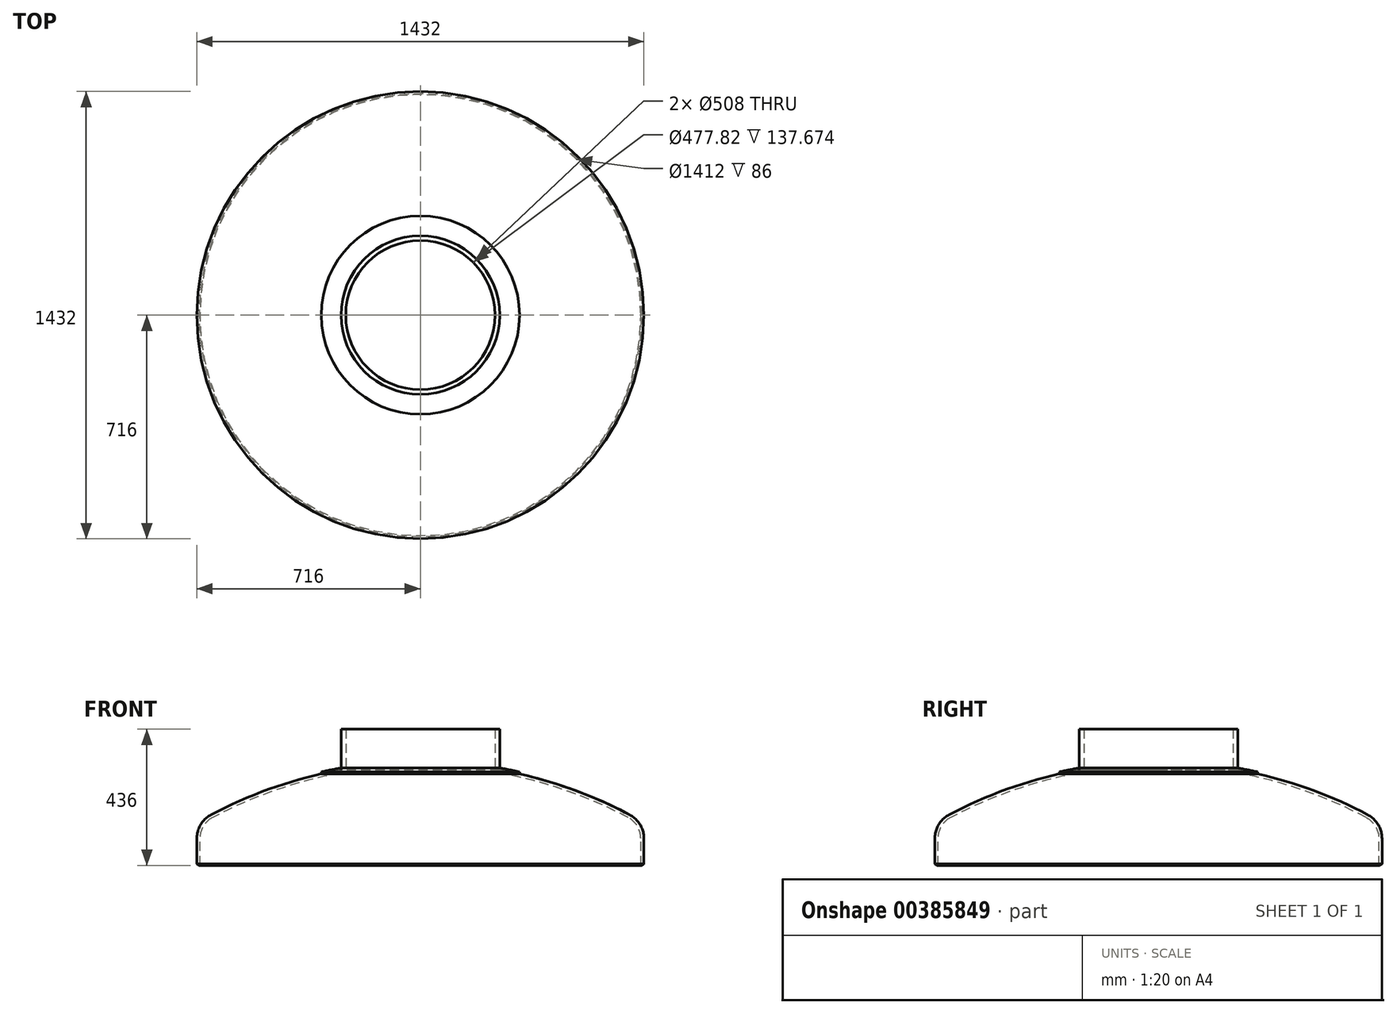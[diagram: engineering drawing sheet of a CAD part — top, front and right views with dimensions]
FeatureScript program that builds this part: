
annotation { "Feature Type Name" : "Feature", "Feature Type Description" : "" }
export const myFeature = defineFeature(function(context is Context, id is Id, definition is map)
    precondition{}
    {
        {
            var Q0;
            Q0=qCreatedBy(makeId("Front.planeOp"),FACE);
            var sketch = newSketch(context, id + "F0", { "sketchPlane" : qUnion([Q0])});
            skArc(sketch, "E0", {"start": v(716, 0) * mm, "mid": v(703.68, 44.35) * mm, "end": v(670.25, 76) * mm});
            skLineSegment(sketch, "E1", {"start": v(0, 140.34) * mm, "end": v(0, -100.1) * mm, "construction": true});
            skArc(sketch, "E2.MirrorCS", {"start": v(-716, 0) * mm, "mid": v(-703.68, 44.35) * mm, "end": v(-670.25, 76) * mm});
            skArc(sketch, "E3", {"start": v(670.25, 76) * mm, "mid": v(0, 242.54) * mm, "end": v(-670.25, 76) * mm});
            skLineSegment(sketch, "E4", {"start": v(-716, 0) * mm, "end": v(716, 0) * mm, "construction": true});
            skPoint(sketch, "E5.orphan", {"position": v(-544, 0) * mm});
            skPoint(sketch, "E6.orphan", {"position": v(544, 0) * mm});
            skLineSegment(sketch, "E7", {"start": v(-716, 0) * mm, "end": v(-716, -86) * mm});
            skLineSegment(sketch, "E8.MirrorCS", {"start": v(716, 0) * mm, "end": v(716, -81.96) * mm});
            skArc(sketch, "E9.0", {"start": v(665.57, 67.16) * mm, "mid": v(0, 232.54) * mm, "end": v(-665.57, 67.16) * mm});
            skArc(sketch, "E10.0", {"start": v(-706, 0) * mm, "mid": v(-695.11, 39.2) * mm, "end": v(-665.57, 67.16) * mm});
            skLineSegment(sketch, "E11.0", {"start": v(-706, 0) * mm, "end": v(-706, -86) * mm});
            skArc(sketch, "E12.MirrorCS", {"start": v(706, 0) * mm, "mid": v(695.11, 39.2) * mm, "end": v(665.57, 67.16) * mm});
            skLineSegment(sketch, "E13.MirrorCS", {"start": v(706, 0) * mm, "end": v(706, -86) * mm});
            skLineSegment(sketch, "E14", {"start": v(-716, -86) * mm, "end": v(-706, -86) * mm});
            skLineSegment(sketch, "E15.MirrorCS", {"start": v(709, -86) * mm, "end": v(706, -86) * mm});
            skLineSegment(sketch, "E16", {"start": v(0, 242.54) * mm, "end": v(0, 232.54) * mm});
            skLineSegment(sketch, "E17", {"start": v(709, -86) * mm, "end": v(716, -81.96) * mm});
            skPoint(sketch, "E18.orphan", {"position": v(716, -86) * mm});
            skCircle(sketch, "E19", {"center": v(0, 0) * mm, "radius": 254 * mm, "construction": true});
            skCircle(sketch, "E20", {"center": v(0, 0) * mm, "radius": 317.5 * mm, "construction": true});
            skLineSegment(sketch, "E21", {"start": v(-317.5, 0) * mm, "end": v(-317.5, 206.9) * mm, "construction": true});
            skLineSegment(sketch, "E22", {"start": v(-254, 0) * mm, "end": v(-254, 219.83) * mm, "construction": true});
            skLineSegment(sketch, "E23.MirrorCS", {"start": v(254, 0) * mm, "end": v(254, 219.83) * mm, "construction": true});
            skLineSegment(sketch, "E24.MirrorCS", {"start": v(317.5, 0) * mm, "end": v(317.5, 206.9) * mm, "construction": true});
            skLineSegment(sketch, "E25", {"start": v(-317.5, 206.9) * mm, "end": v(-317.5, 213.05) * mm});
            skLineSegment(sketch, "E26", {"start": v(-254, 219.83) * mm, "end": v(-254, 225.93) * mm});
            skArc(sketch, "E27.trimOffspring", {"start": v(-254, 225.93) * mm, "mid": v(-285.82, 219.85) * mm, "end": v(-317.5, 213.05) * mm});
            skLineSegment(sketch, "E28", {"start": v(0, 232.54) * mm, "end": v(0, 0) * mm});
            skLineSegment(sketch, "E29", {"start": v(0, 0) * mm, "end": v(706, 0) * mm});
            skSolve(sketch);
        }
        {
            var Q0;
            Q0=makeQuery(id+"F0.imprint","IMPRINT",FACE,{"disambiguationData":[TD([[makeQuery(id+"F0.imprint","IMPRINT",EDGE,{"derivedFrom":sQuery(id+"F0.wireOp",EDGE,"E0")}),1.0]])]});
            var Q1;
            Q1=sQuery(id+"F0.wireOp",EDGE,"E1");
            revolve(context, id + "F1", {"entities" : qUnion([Q0]), "axis" : qUnion([Q1]), "revolveType" : RevolveType.FULL});
        }
        {
            var Q0;
            {var subQ0=sQuery(id+"F0.wireOp",EDGE,"E25");Q0=makeQuery(id+"F0.imprint","IMPRINT",FACE,{"disambiguationData":[TD([[makeQuery(id+"F0.imprint","IMPRINT",EDGE,{"derivedFrom":subQ0}),-1.0]])]});}
            var Q1;
            Q1=sQuery(id+"F0.wireOp",EDGE,"E1");
            revolve(context, id + "F2", {"entities" : qUnion([Q0]), "axis" : qUnion([Q1]), "revolveType" : RevolveType.FULL});
        }
        {
            var Q0;
            Q0=qCreatedBy(makeId("Top.planeOp"),FACE);
            var sketch = newSketch(context, id + "F3", { "sketchPlane" : qUnion([Q0])});
            skCircle(sketch, "E30", {"center": v(0, 0) * mm, "radius": 254 * mm});
            skCircle(sketch, "E31", {"center": v(0, 0) * mm, "radius": 238.91 * mm});
            skSolve(sketch);
        }
        {
            var Q0;
            Q0=makeQuery(id+"F3.imprint","IMPRINT",FACE,{"disambiguationData":[TD([[makeQuery(id+"F3.imprint","IMPRINT",EDGE,{"derivedFrom":sQuery(id+"F3.wireOp",EDGE,"E31")}),1.0]])]});
            var Q1;
            Q1=makeQuery(id+"F3.imprint","IMPRINT",FACE,{"disambiguationData":[TD([[makeQuery(id+"F3.imprint","IMPRINT",EDGE,{"derivedFrom":sQuery(id+"F3.wireOp",EDGE,"E30")}),1.0]])]});
            extrude(context, id + "F4", {"entities" : qUnion([Q0, Q1]), "operationType" : NewBodyOperationType.REMOVE, "endBound" : BoundingType.THROUGH_ALL, "depth" : 25 * mm});
        }
        {
            var Q0;
            Q0=makeQuery(id+"F3.imprint","IMPRINT",FACE,{"disambiguationData":[TD([[makeQuery(id+"F3.imprint","IMPRINT",EDGE,{"derivedFrom":sQuery(id+"F3.wireOp",EDGE,"E30")}),1.0]])]});
            extrude(context, id + "F5", {"entities" : qUnion([Q0]), "depth" : 350 * mm});
        }
        {
            var Q0;
            {var subQ0=sQuery(id+"F0.wireOp",EDGE,"E12.MirrorCS");Q0=makeQuery(id+"F0.imprint","IMPRINT",FACE,{"disambiguationData":[TD([[makeQuery(id+"F0.imprint","IMPRINT",EDGE,{"derivedFrom":subQ0}),1.0]])]});}
            var Q1;
            Q1=sQuery(id+"F0.wireOp",EDGE,"E28");
            revolve(context, id + "F6", {"operationType" : NewBodyOperationType.REMOVE, "entities" : qUnion([Q0]), "axis" : qUnion([Q1]), "revolveType" : RevolveType.FULL, "oppositeDirection" : true});
        }
    });
